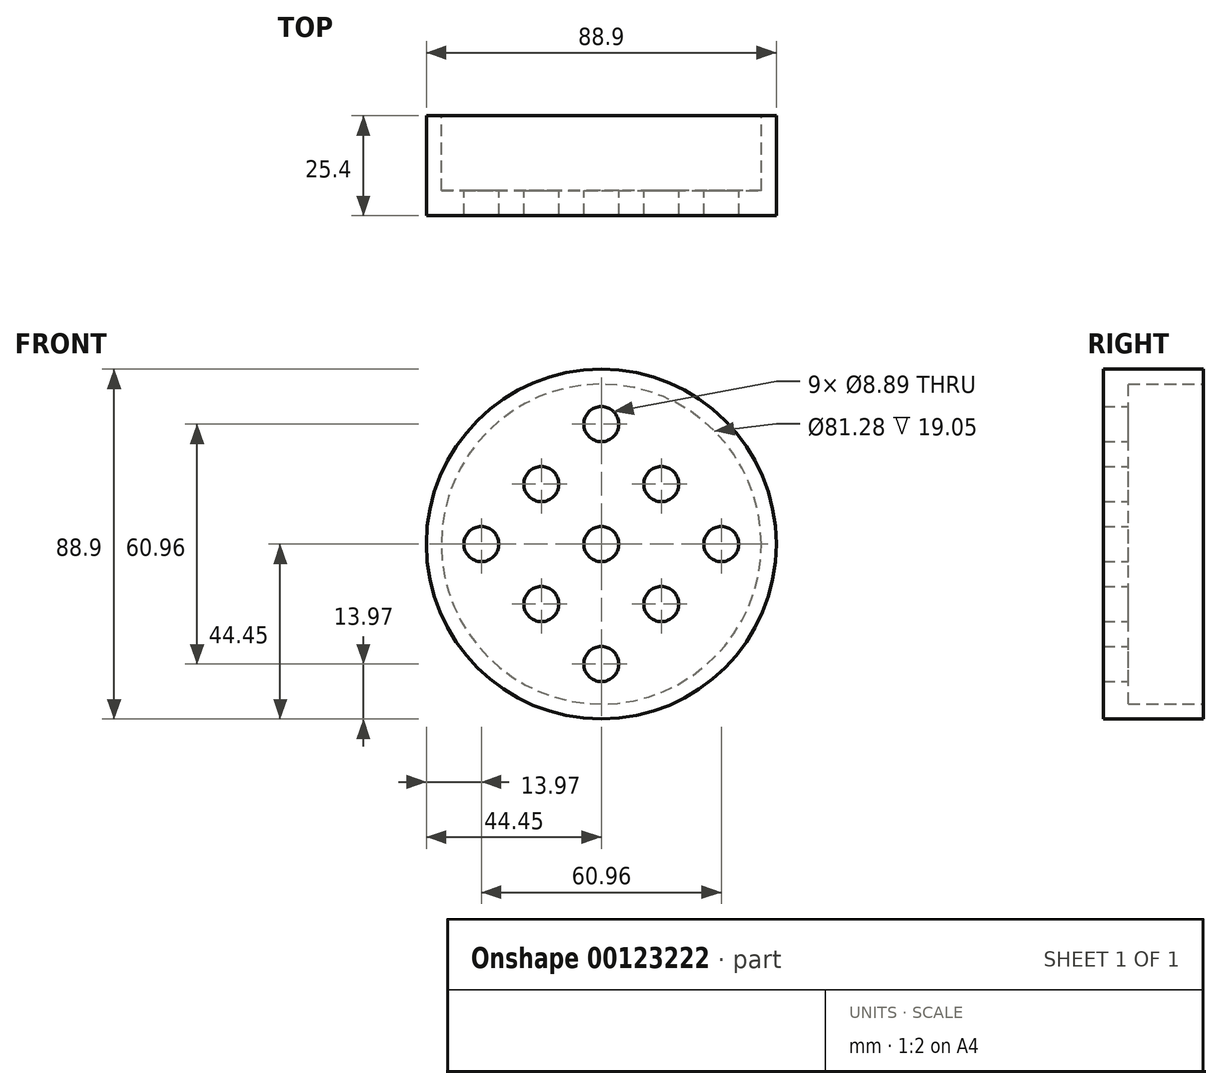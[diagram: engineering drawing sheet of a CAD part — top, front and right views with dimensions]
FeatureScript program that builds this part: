
annotation { "Feature Type Name" : "Feature", "Feature Type Description" : "" }
export const myFeature = defineFeature(function(context is Context, id is Id, definition is map)
    precondition{}
    {
        {
            var Q0;
            Q0=qCreatedBy(makeId("Front.planeOp"),FACE);
            var sketch = newSketch(context, id + "F0", { "sketchPlane" : qUnion([Q0])});
            skCircle(sketch, "E0", {"center": v(0, 0) * mm, "radius": 44.45 * mm});
            skSolve(sketch);
        }
        {
            var Q0;
            Q0 = qSketchRegion(id + "F0", true);
            extrude(context, id + "F1", {"entities" : qUnion([Q0]), "depth" : 25.4 * mm});
        }
        {
            var Q0;
            Q0=qCreatedBy(makeId("Front.planeOp"),FACE);
            var sketch = newSketch(context, id + "F2", { "sketchPlane" : qUnion([Q0])});
            skCircle(sketch, "E1", {"center": v(0, 0) * mm, "radius": 40.64 * mm});
            skSolve(sketch);
        }
        {
            var Q0;
            Q0 = qSketchRegion(id + "F2", true);
            extrude(context, id + "F3", {"entities" : qUnion([Q0]), "operationType" : NewBodyOperationType.REMOVE, "depth" : 19.05 * mm});
        }
        {
            var Q0;
            Q0=qCreatedBy(makeId("Front.planeOp"),FACE);
            var sketch = newSketch(context, id + "F4", { "sketchPlane" : qUnion([Q0])});
            skPoint(sketch, "E2", {"position": v(0, 30.48) * mm});
            skPoint(sketch, "E3", {"position": v(0, -30.48) * mm});
            skPoint(sketch, "E4", {"position": v(-30.48, 0) * mm});
            skPoint(sketch, "E5", {"position": v(30.48, 0) * mm});
            skPoint(sketch, "E6", {"position": v(-15.24, 15.24) * mm});
            skPoint(sketch, "E7", {"position": v(-15.24, -15.24) * mm});
            skPoint(sketch, "E8", {"position": v(15.24, -15.24) * mm});
            skPoint(sketch, "E9", {"position": v(15.24, 15.24) * mm});
            skPoint(sketch, "E10", {"position": v(-15.24, 0) * mm});
            skPoint(sketch, "E11", {"position": v(15.24, 0) * mm});
            skPoint(sketch, "E12", {"position": v(0, -15.24) * mm});
            skCircle(sketch, "E13", {"center": v(0, 30.48) * mm, "radius": 4.45 * mm});
            skCircle(sketch, "E14", {"center": v(-15.24, 15.24) * mm, "radius": 4.45 * mm});
            skCircle(sketch, "E15", {"center": v(-30.48, 0) * mm, "radius": 4.45 * mm});
            skCircle(sketch, "E16", {"center": v(15.24, 15.24) * mm, "radius": 4.45 * mm});
            skCircle(sketch, "E17", {"center": v(30.48, 0) * mm, "radius": 4.45 * mm});
            skCircle(sketch, "E18", {"center": v(-15.24, -15.24) * mm, "radius": 4.45 * mm});
            skCircle(sketch, "E19", {"center": v(15.24, -15.24) * mm, "radius": 4.45 * mm});
            skCircle(sketch, "E20", {"center": v(0, -30.48) * mm, "radius": 4.45 * mm});
            skCircle(sketch, "E21", {"center": v(0, 0) * mm, "radius": 4.45 * mm});
            skSolve(sketch);
        }
        {
            var Q0;
            Q0 = qSketchRegion(id + "F4", true);
            var Q1;
            Q1=sQuery(id+"F4.wireOp",EDGE,"E15");
            var Q2;
            Q2=sQuery(id+"F4.wireOp",EDGE,"E14");
            var Q3;
            Q3=sQuery(id+"F4.wireOp",EDGE,"E13");
            var Q4;
            Q4=sQuery(id+"F4.wireOp",EDGE,"E16");
            var Q5;
            Q5=sQuery(id+"F4.wireOp",EDGE,"E17");
            var Q6;
            Q6=sQuery(id+"F4.wireOp",EDGE,"E19");
            var Q7;
            Q7=sQuery(id+"F4.wireOp",EDGE,"E20");
            var Q8;
            Q8=sQuery(id+"F4.wireOp",EDGE,"E18");
            var Q9;
            Q9=sQuery(id+"F4.wireOp",EDGE,"E21");
            extrude(context, id + "F5", {"entities" : qUnion([Q0]), "operationType" : NewBodyOperationType.REMOVE, "surfaceEntities" : qUnion([Q1, Q2, Q3, Q4, Q5, Q6, Q7, Q8, Q9]), "depth" : 25.4 * mm});
        }
    });
